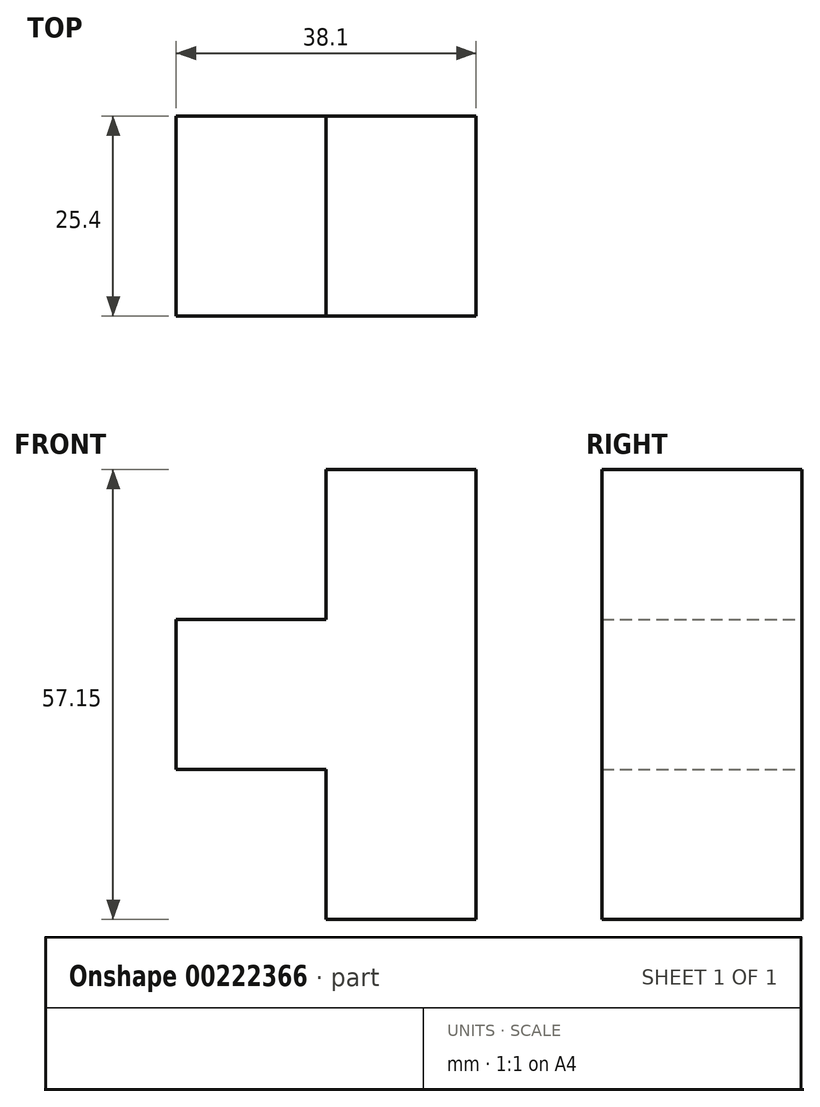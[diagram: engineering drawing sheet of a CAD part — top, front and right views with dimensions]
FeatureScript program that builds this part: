
annotation { "Feature Type Name" : "Feature", "Feature Type Description" : "" }
export const myFeature = defineFeature(function(context is Context, id is Id, definition is map)
    precondition{}
    {
        {
            var Q0;
            Q0=qCreatedBy(makeId("Front.planeOp"),FACE);
            var sketch = newSketch(context, id + "F0", { "sketchPlane" : qUnion([Q0])});
            skLineSegment(sketch, "E0.bottom", {"start": v(-34.3, 14.62) * mm, "end": v(-53.36, 14.62) * mm});
            skLineSegment(sketch, "E0.top", {"start": v(-34.3, 71.77) * mm, "end": v(-53.36, 71.77) * mm});
            skLineSegment(sketch, "E0.left", {"start": v(-34.3, 14.62) * mm, "end": v(-34.3, 71.77) * mm});
            skLineSegment(sketch, "E0.right", {"start": v(-53.36, 14.62) * mm, "end": v(-53.36, 71.77) * mm});
            skPoint(sketch, "E0.middle", {"position": v(-43.83, 43.2) * mm});
            skLineSegment(sketch, "E1.bottom", {"start": v(-53.36, 33.7) * mm, "end": v(-72.4, 33.7) * mm});
            skLineSegment(sketch, "E1.top", {"start": v(-53.36, 52.74) * mm, "end": v(-72.4, 52.74) * mm});
            skLineSegment(sketch, "E1.left", {"start": v(-53.36, 33.7) * mm, "end": v(-53.36, 52.74) * mm});
            skLineSegment(sketch, "E1.right", {"start": v(-72.4, 33.7) * mm, "end": v(-72.4, 52.74) * mm});
            skPoint(sketch, "E1.middle", {"position": v(-62.88, 43.22) * mm});
            skSolve(sketch);
        }
        {
            var Q0;
            Q0 = qSketchRegion(id + "F0", true);
            extrude(context, id + "F1", {"entities" : qUnion([Q0]), "depth" : 25.4 * mm});
        }
    });
